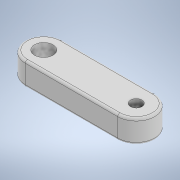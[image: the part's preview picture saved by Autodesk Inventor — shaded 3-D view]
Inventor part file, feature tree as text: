
AUTODESK INVENTOR PART (.ipt)
format: ipt  version: 2021 (Build 250183000, 183)  size: 133,120 bytes
history: native  units: mm
features: extrude x1, fillet x1, sketch x1
ambient origin geometry x8: Origin, YZ Plane, XZ Plane, XY Plane, X Axis, Y Axis, Z Axis, Center Point
bodies: Solid1 (feature_tree)
feature tree (3):
  extrude  "Extrusion1"  Depth=13.33mm
  fillet  "Fillet1"  Radius=2.66mm
  sketch  "Sketch1"  dims[d0=5.33mm d1=13.33mm d2=2.66mm d3=1.66mm d4=3.33mm d5=0.0mm d6=0.33mm d7=0.872665mm]
